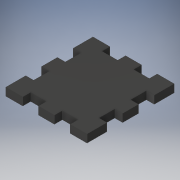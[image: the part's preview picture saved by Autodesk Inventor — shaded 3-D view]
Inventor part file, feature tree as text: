
AUTODESK INVENTOR PART (.ipt)
format: ipt  version: 2019 (Build 230136000, 136)  size: 158,208 bytes
history: native  units: mm
features: extrude x2, sketch x2
ambient origin geometry x8: Origin, YZ Plane, XZ Plane, XY Plane, X Axis, Y Axis, Z Axis, Center Point
bodies: Solid1 (feature_tree)
feature tree (4):
  extrude  "Extrusion1"  Depth=44.0mm
  extrude  "Extrusion2"  Depth=4.0mm
  sketch  "Sketch1"  dims[d0=41.0mm d1=44.0mm]
  sketch  "Sketch2"  dims[d6=4.0mm d7=0.0mm d8=4.0mm d9=8.0mm d10=4.0mm d11=8.0mm d12=4.0mm d13=4.0mm d14=0.0mm]
